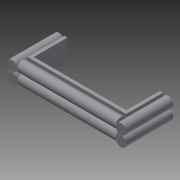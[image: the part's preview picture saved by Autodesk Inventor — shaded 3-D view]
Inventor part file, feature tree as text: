
AUTODESK INVENTOR PART (.ipt)
format: ipt  version: 2014 SP1 (Build 180222100, 222)  size: 138,240 bytes
history: native  units: in
note: dims shown in document units (in); Inventor stores cm internally (conversion verified against a paired STEP export)
features: extrude x4, sketch x4
ambient origin geometry x8: Origin, YZ Plane, XZ Plane, XY Plane, X Axis, Y Axis, Z Axis, Center Point
bodies: Solid1 (feature_tree)
feature tree (8):
  extrude  "Extrusion1"  Depth=23.5in
  extrude  "Extrusion2"  Depth=0.75in
  extrude  "Extrusion3"  Depth=8.0in TaperAngle=0.0deg
  extrude  "Extrusion4"  Depth=2.5in
  sketch  "Sketch1"  dims[d0=5.0in d1=23.5in]
  sketch  "Sketch2"  dims[d2=0.75in d3=0.0in d4=0.75in]
  sketch  "Sketch3"  dims[d5=0.75in d6=8.0in d7=0.0in]
  sketch  "Sketch4"  dims[d8=2.5in d9=2.5in d10=1.25in d11=1.25in d12=1.25in d13=23.5in d14=0.0in d15=2.5in d16=2.5in d17=26.0in d18=1.25in d19=1.25in d20=11.25in d21=0.0in]
